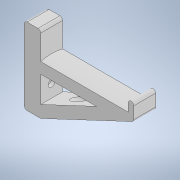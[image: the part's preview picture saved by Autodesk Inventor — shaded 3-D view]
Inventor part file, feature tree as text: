
AUTODESK INVENTOR PART (.ipt)
format: ipt  version: 2022 (Build 260153000, 153)  size: 152,576 bytes
history: native  units: in
note: dims shown in document units (in); Inventor stores cm internally (conversion verified against a paired STEP export)
features: extrude x3, sketch x3, projected_geometry x2, hole x1, fillet x1
ambient origin geometry x8: Origin, YZ Plane, XZ Plane, XY Plane, X Axis, Y Axis, Z Axis, Center Point
bodies: Solid1 (feature_tree)
feature tree (10):
  extrude  "Extrusion1"  Depth=3.1496in
  sketch  "Sketch2"  dims[d2=2.7559in d3=0.9843in]
  extrude  "Extrusion2"  Depth=2.7559in
  hole  "Hole1"  [1 undecoded]
  extrude  "Extrusion3"  Depth=0.3937in
  fillet  "Fillet1"  [1 undecoded]
  sketch  "Sketch1"  dims[d0=0.1969in d1=3.1496in]
  projected_geometry  "Projected Loop1"
  sketch  "Sketch3"  dims[d4=0.5906in d5=0.5906in d6=0.3937in d7=135.0deg d8=0.3937in d9=0.3937in d10=0.5906in d11=0.7874in d12=0.0in d13=0.315in d14=0.315in d19=2.8248in d20=0.0in d21=0.134in d22=0.75in d23=0.256in d24=0.134in d25=0.5635in d26=1.0in d27=0.8108in d28=3.0in d29=2.8248in d30=0.0in d31=0.0984in]
  projected_geometry  "Projected Loop2"
note: 2 required parameter values undecoded (feature->parameter linkage not recoverable at this tier; creation-order binding heuristic only, values carry confidence <= 0.55)
